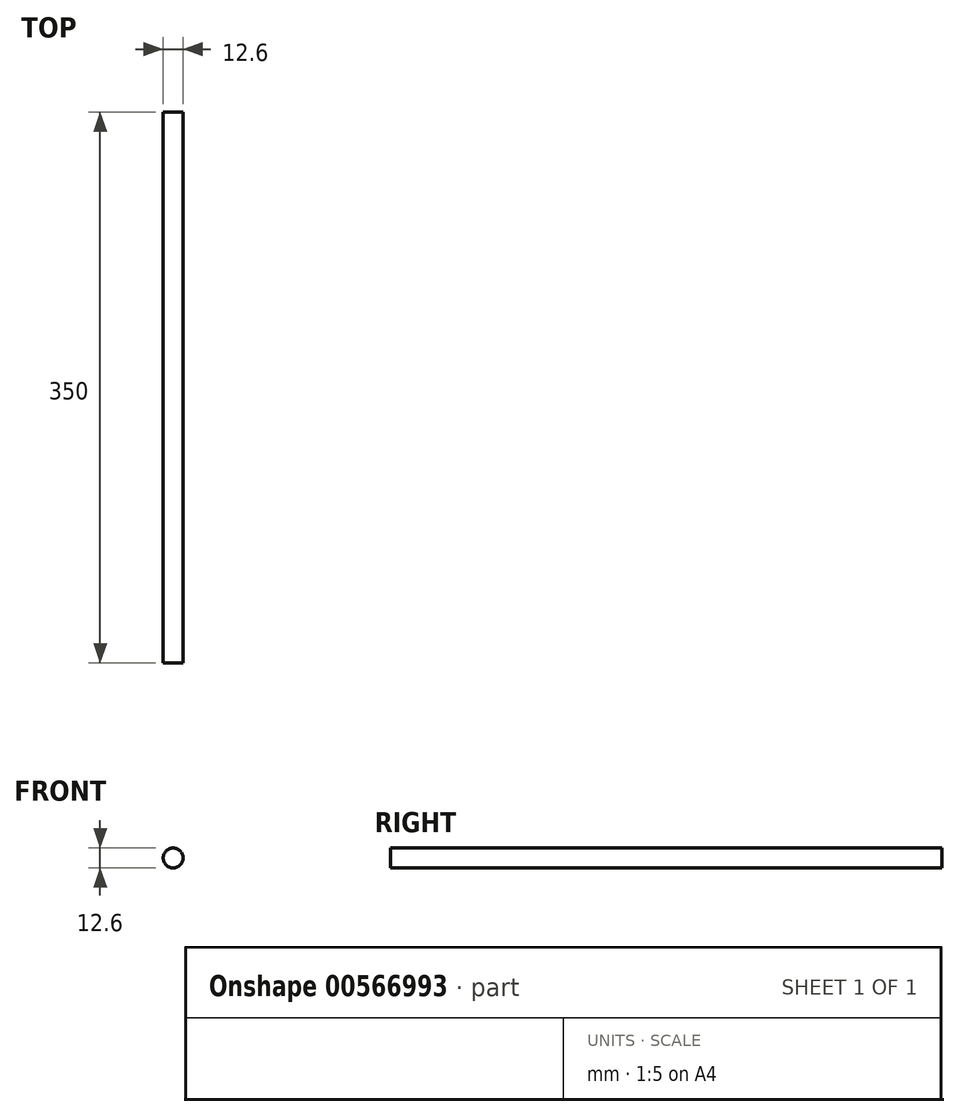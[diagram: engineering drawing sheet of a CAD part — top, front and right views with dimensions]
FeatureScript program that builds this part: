
annotation { "Feature Type Name" : "Feature", "Feature Type Description" : "" }
export const myFeature = defineFeature(function(context is Context, id is Id, definition is map)
    precondition{}
    {
        {
            var Q0;
            Q0=qCreatedBy(makeId("Front.planeOp"),FACE);
            var sketch = newSketch(context, id + "F0", { "sketchPlane" : qUnion([Q0])});
            skCircle(sketch, "E0", {"center": v(0, 0) * mm, "radius": 6.3 * mm});
            skSolve(sketch);
        }
        {
            var Q0;
            Q0=makeQuery(id+"F0.imprint","IMPRINT",FACE,{"disambiguationData":[TD([[makeQuery(id+"F0.imprint","IMPRINT",EDGE,{"derivedFrom":sQuery(id+"F0.wireOp",EDGE,"E0")}),1.0]])]});
            extrude(context, id + "F1", {"entities" : qUnion([Q0]), "depth" : 350 * mm, "offsetDistance" : 25 * mm});
        }
    });
